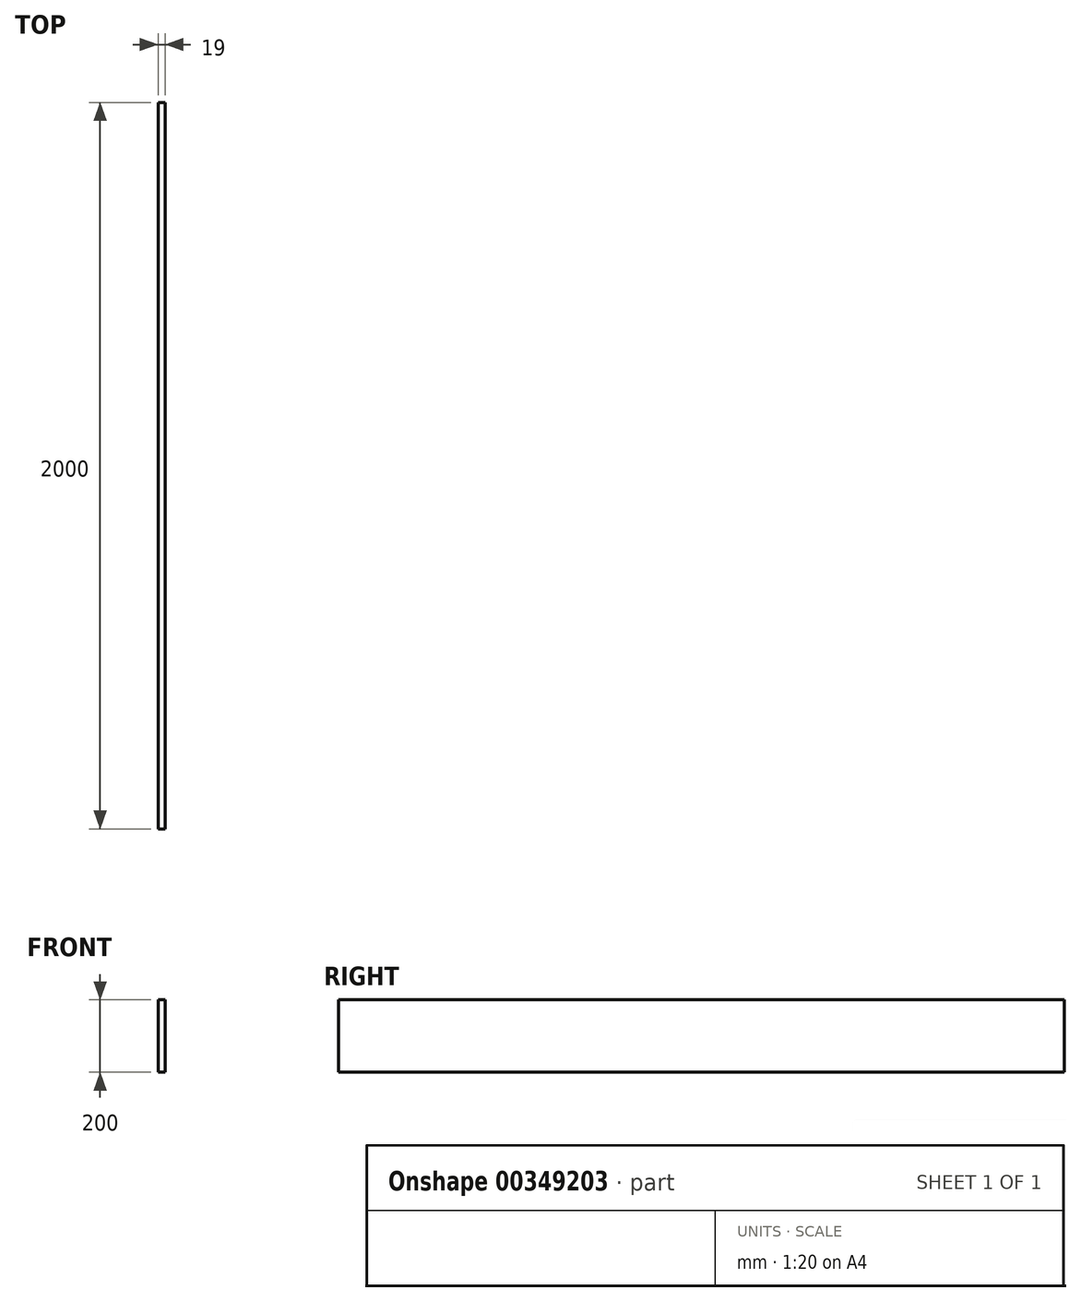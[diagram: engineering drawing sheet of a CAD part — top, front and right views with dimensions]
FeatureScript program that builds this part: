
annotation { "Feature Type Name" : "Feature", "Feature Type Description" : "" }
export const myFeature = defineFeature(function(context is Context, id is Id, definition is map)
    precondition{}
    {
        {
            var Q0;
            Q0=qCreatedBy(makeId("Right.planeOp"),FACE);
            var sketch = newSketch(context, id + "F0", { "sketchPlane" : qUnion([Q0])});
            skLineSegment(sketch, "E0.bottom", {"start": v(0, 0) * mm, "end": v(2000, 0) * mm});
            skLineSegment(sketch, "E0.top", {"start": v(0, 200) * mm, "end": v(2000, 200) * mm});
            skLineSegment(sketch, "E0.left", {"start": v(0, 0) * mm, "end": v(0, 200) * mm});
            skLineSegment(sketch, "E0.right", {"start": v(2000, 0) * mm, "end": v(2000, 200) * mm});
            skSolve(sketch);
        }
        {
            var Q0;
            Q0=makeQuery(id+"F0.imprint","IMPRINT",FACE,{"disambiguationData":[TD([[makeQuery(id+"F0.imprint","IMPRINT",EDGE,{"derivedFrom":sQuery(id+"F0.wireOp",EDGE,"E0.bottom")}),1.0]])]});
            extrude(context, id + "F1", {"entities" : qUnion([Q0]), "depth" : 19 * mm});
        }
    });
